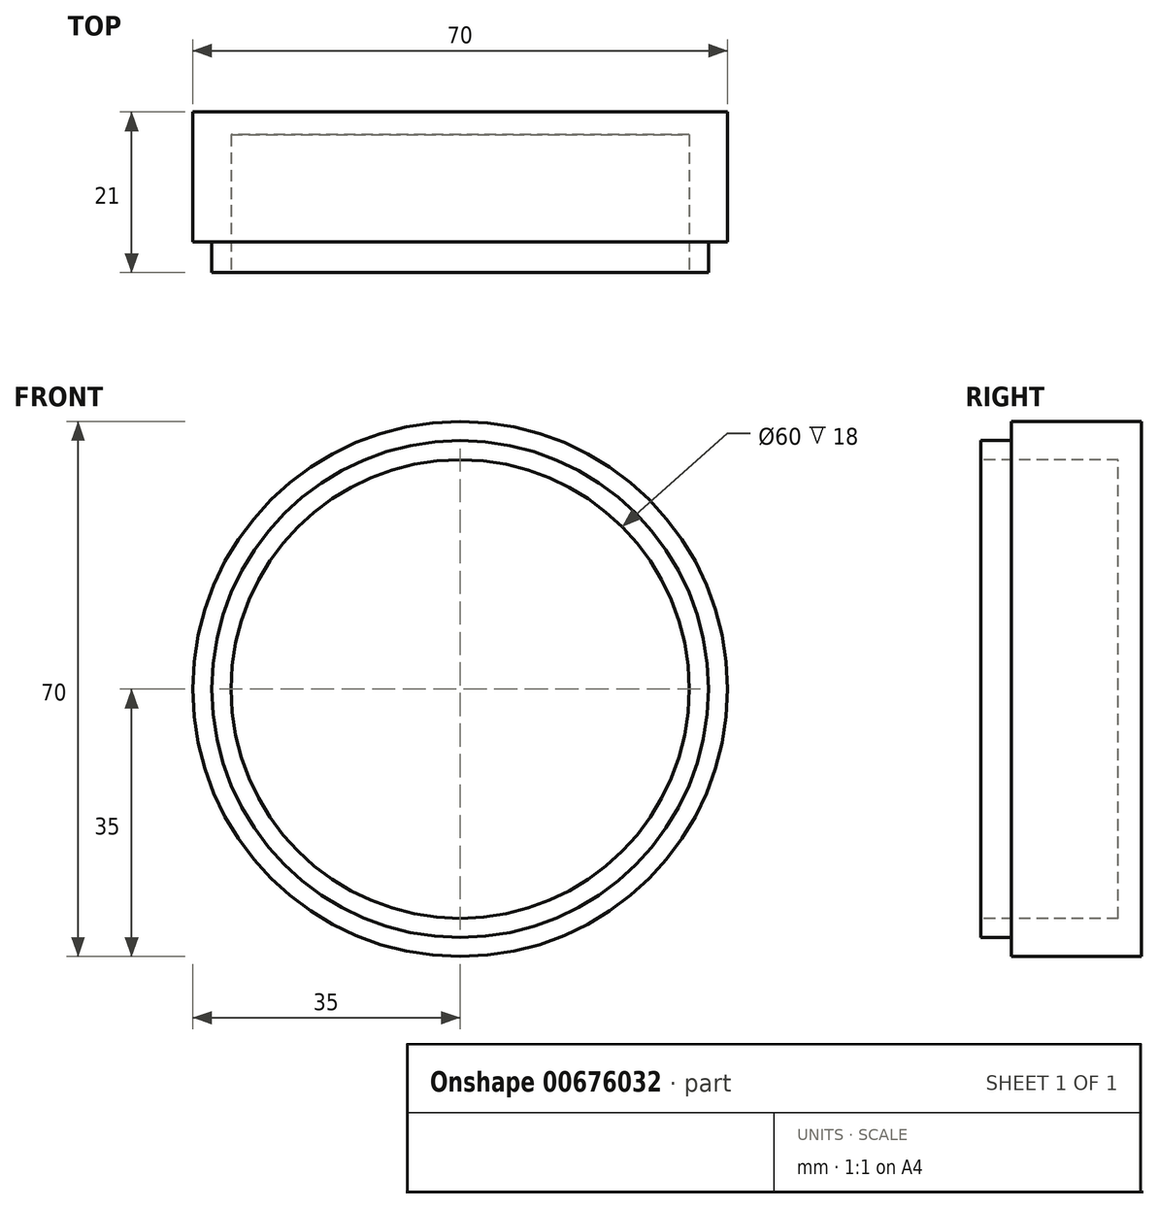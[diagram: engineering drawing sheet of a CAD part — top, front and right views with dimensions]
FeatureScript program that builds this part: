
annotation { "Feature Type Name" : "Feature", "Feature Type Description" : "" }
export const myFeature = defineFeature(function(context is Context, id is Id, definition is map)
    precondition{}
    {
        {
            var Q0;
            Q0=qCreatedBy(makeId("Front.planeOp"),FACE);
            var sketch = newSketch(context, id + "F0", { "sketchPlane" : qUnion([Q0])});
            skCircle(sketch, "E0", {"center": v(0, 0) * mm, "radius": 35 * mm});
            skSolve(sketch);
        }
        {
            var Q0;
            Q0 = qSketchRegion(id + "F0", true);
            extrude(context, id + "F1", {"entities" : qUnion([Q0]), "depth" : 21 * mm, "offsetDistance" : 25 * mm});
        }
        {
            var Q0;
            Q0=makeQuery(id+"F1.opExtrude","CAP_FACE",FACE,{"disambiguationData":[OSD([sQuery(id+"F0.wireOp",EDGE,"E0")])],"isStart":false});
            var sketch = newSketch(context, id + "F2", { "sketchPlane" : qUnion([Q0])});
            skCircle(sketch, "E1", {"center": v(0, 0) * mm, "radius": 30 * mm});
            skSolve(sketch);
        }
        {
            var Q0;
            Q0=makeQuery(id+"F2.imprint","IMPRINT",FACE,{"disambiguationData":[TD([[makeQuery(id+"F2.imprint","IMPRINT",EDGE,{"derivedFrom":sQuery(id+"F2.wireOp",EDGE,"E1")}),1.0]])]});
            extrude(context, id + "F3", {"entities" : qUnion([Q0]), "operationType" : NewBodyOperationType.REMOVE, "oppositeDirection" : true, "depth" : 18 * mm, "offsetDistance" : 25 * mm});
        }
        {
            var Q0;
            Q0=makeQuery(id+"F2.imprint","IMPRINT",FACE,{"disambiguationData":[TD([[makeQuery(id+"F2.imprint","IMPRINT",EDGE,{"derivedFrom":sQuery(id+"F2.wireOp",EDGE,"E1")}),-1.0]])]});
            var sketch = newSketch(context, id + "F4", { "sketchPlane" : qUnion([Q0])});
            skCircle(sketch, "E2", {"center": v(0, 0) * mm, "radius": 32.5 * mm});
            skSolve(sketch);
        }
        {
            var Q0;
            Q0=makeQuery(id+"F4.imprint","IMPRINT",FACE,{"disambiguationData":[TD([[makeQuery(id+"F4.imprint","IMPRINT",EDGE,{"derivedFrom":sQuery(id+"F4.wireOp",EDGE,"E2")}),-1.0]])]});
            extrude(context, id + "F5", {"entities" : qUnion([Q0]), "operationType" : NewBodyOperationType.REMOVE, "oppositeDirection" : true, "depth" : 4 * mm, "offsetDistance" : 25 * mm});
        }
    });
